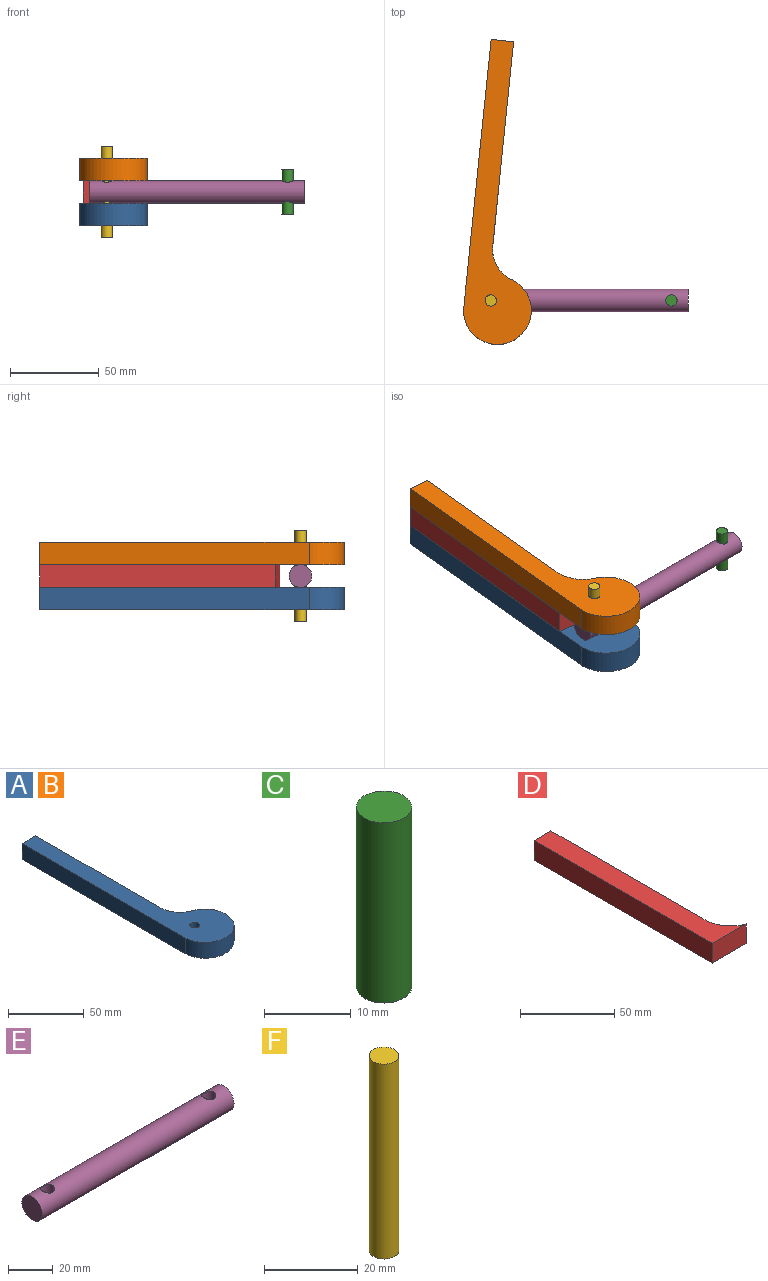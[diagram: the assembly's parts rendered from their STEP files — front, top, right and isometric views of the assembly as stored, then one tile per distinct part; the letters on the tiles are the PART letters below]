
ASSEMBLY  parts=6 mates=5
PART A: 8 faces, bbox 38.1x170.4x12.7 mm
  f0: plane 152.4x12.7mm, normal (-1,0,0), area 1935.5mm2, adj f1,f4,f6,f7
  f1: cylinder r=19.05mm len=38.07mm, axis (0,0,-1), area 1043.8mm2, adj f0,f2,f6,f7
  f2: cylinder r=19.05mm len=19.07mm, axis (0,0,-1), area 312.2mm2, adj f1,f3,f6,f7
  f3: plane 114.3x12.7mm, normal (1,0,0), area 1451.6mm2, adj f2,f4,f6,f7
  f4: plane 12.7x12.7mm, normal (0,1,0), area 161.3mm2, adj f0,f3,f6,f7
  f5: cylinder r=3.17mm len=12.7mm, axis (0,0,-1), area 253.4mm2, adj f6,f7
  f6: plane 170.37x38.07mm, normal (0,0,1), area 2915.2mm2, adj f0,f1,f2,f3,f4,f5
  f7: plane 170.37x38.07mm, normal (0,0,-1), area 2915.2mm2, adj f0,f1,f2,f3,f4,f5
PART B: same geometry as A
PART C: 3 faces, bbox 6.4x6.4x25.4 mm
  f0: cylinder r=3.17mm len=25.4mm, axis (0,0,-1), area 506.7mm2, adj f1,f2
  f1: plane 6.35x6.35mm, normal (0,0,1), area 31.7mm2, adj f0
  f2: plane 6.35x6.35mm, normal (0,0,-1), area 31.7mm2, adj f0
PART D: 7 faces, bbox 25.4x133.4x12.7 mm
  f0: plane 114.3x12.7mm, normal (1,0,0), area 1451.6mm2, adj f1,f4,f5,f6
  f1: plane 12.7x12.7mm, normal (0,1,0), area 161.3mm2, adj f0,f2,f5,f6
  f2: plane 133.35x12.7mm, normal (-1,0,0), area 1693.5mm2, adj f1,f3,f5,f6
  f3: plane 25.4x12.7mm, normal (0,-1,0), area 322.6mm2, adj f2,f4,f5,f6
  f4: cylinder r=19.05mm len=19.05mm, axis (0,0,-1), area 311.9mm2, adj f0,f3,f5,f6
  f5: plane 133.35x25.4mm, normal (0,0,1), area 1754.9mm2, adj f0,f1,f2,f3,f4
  f6: plane 133.35x25.4mm, normal (0,0,-1), area 1754.9mm2, adj f0,f1,f2,f3,f4
PART E: 5 faces, bbox 120.7x12.7x12.7 mm
  f0: cylinder r=6.35mm len=120.65mm, axis (-1,0,0), area 4682.8mm2, adj f1,f2,f3,f4
  f1: plane 12.7x12.7mm, normal (1,0,0), area 126.7mm2, adj f0
  f2: plane 12.7x12.7mm, normal (-1,0,0), area 126.7mm2, adj f0
  f3: cylinder r=3.17mm len=12.7mm, axis (0,0,1), area 236.7mm2, adj f0
  f4: cylinder r=3.17mm len=12.7mm, axis (0,0,1), area 236.7mm2, adj f0
PART F: 3 faces, bbox 6.4x6.4x50.8 mm
  f0: cylinder r=3.17mm len=50.8mm, axis (0,0,-1), area 1013.4mm2, adj f1,f2
  f1: plane 6.35x6.35mm, normal (0,0,1), area 31.7mm2, adj f0
  f2: plane 6.35x6.35mm, normal (0,0,-1), area 31.7mm2, adj f0
PLACE A rot(axis=(0,0,-1),5.8deg) t=(18.31,-8.25,6.35)mm
PLACE B rot(axis=(0,0,-1),5.8deg) t=(18.31,-8.25,31.75)mm
PLACE C t=(101.6,0,12.7)mm
PLACE D rot(axis=(0,0,-1),5.8deg) t=(-13.33,14.13,19.05)mm
PLACE E t=(50.8,0,25.4)mm
PLACE F rot(axis=(0,0,-1),5.8deg) t=(0,0,0)mm
MATE fastened A.f6 <-> D.f6  axis (0,0,1) through (0.22,146.79,19.05)mm
MATE fastened F.f0 <-> A.f5  axis (0,0,-1) through (0,0,0)mm
MATE revolute F.f0 <-> E.f4  axis (0,0,-1) through (0,0,25.4)mm
MATE fastened E.f3 <-> C.f0  axis (0,0,1) through (101.6,0,25.4)mm
MATE fastened D.f5 <-> B.f7  axis (0,0,1) through (0.22,146.79,31.75)mm
